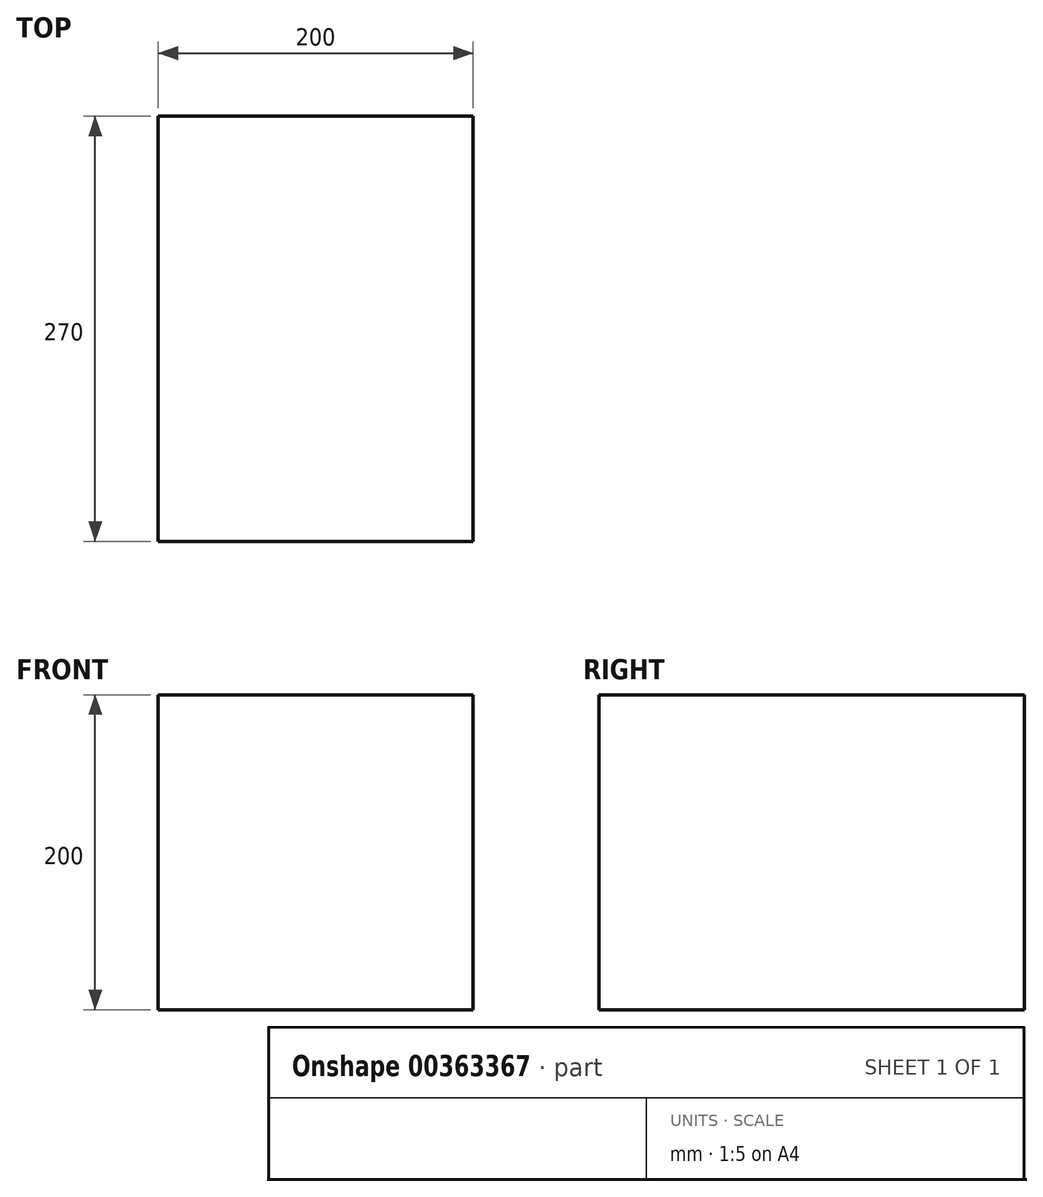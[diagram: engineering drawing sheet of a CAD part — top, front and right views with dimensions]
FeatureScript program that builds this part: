
annotation { "Feature Type Name" : "Feature", "Feature Type Description" : "" }
export const myFeature = defineFeature(function(context is Context, id is Id, definition is map)
    precondition{}
    {
        {
            var Q0;
            Q0=qCreatedBy(makeId("Top.planeOp"),FACE);
            var sketch = newSketch(context, id + "F0", { "sketchPlane" : qUnion([Q0])});
            skLineSegment(sketch, "E0.bottom", {"start": v(0, 0) * mm, "end": v(200, 0) * mm});
            skLineSegment(sketch, "E0.top", {"start": v(0, 270) * mm, "end": v(200, 270) * mm});
            skLineSegment(sketch, "E0.left", {"start": v(0, 0) * mm, "end": v(0, 270) * mm});
            skLineSegment(sketch, "E0.right", {"start": v(200, 0) * mm, "end": v(200, 270) * mm});
            skSolve(sketch);
        }
        {
            var Q0;
            Q0=makeQuery(id+"F0.imprint","IMPRINT",FACE,{"disambiguationData":[TD([[makeQuery(id+"F0.imprint","IMPRINT",EDGE,{"derivedFrom":sQuery(id+"F0.wireOp",EDGE,"E0.bottom")}),1.0]])]});
            extrude(context, id + "F1", {"entities" : qUnion([Q0]), "depth" : 200 * mm});
        }
    });
